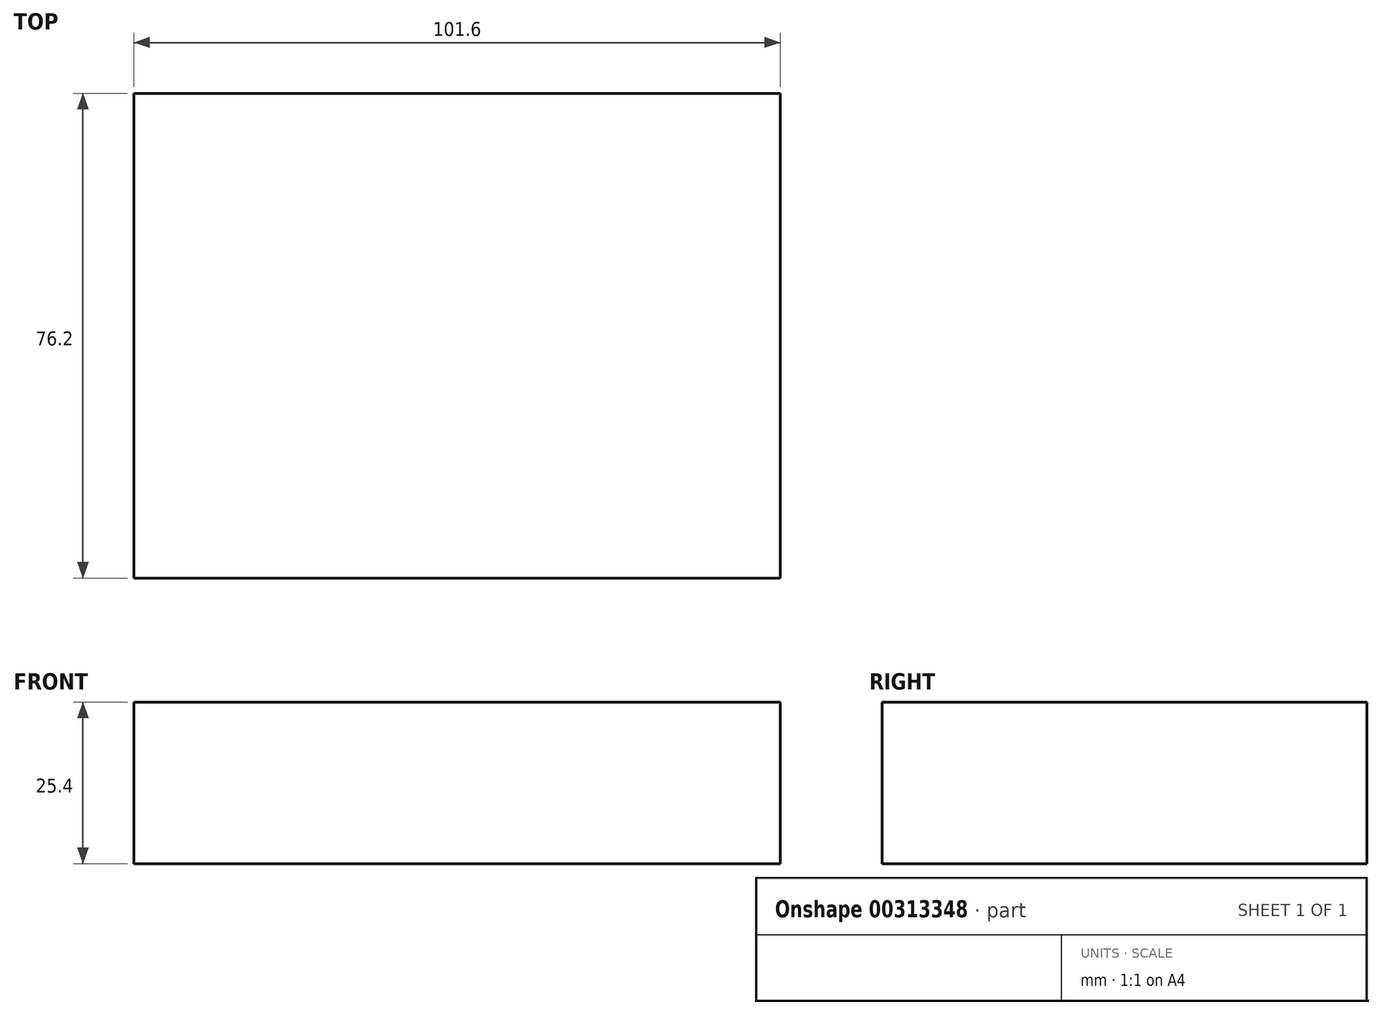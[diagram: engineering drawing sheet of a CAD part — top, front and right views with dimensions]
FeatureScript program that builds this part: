
annotation { "Feature Type Name" : "Feature", "Feature Type Description" : "" }
export const myFeature = defineFeature(function(context is Context, id is Id, definition is map)
    precondition{}
    {
        {
            var Q0;
            Q0=qCreatedBy(makeId("Front.planeOp"),FACE);
            var sketch = newSketch(context, id + "F0", { "sketchPlane" : qUnion([Q0])});
            skLineSegment(sketch, "E0", {"start": v(-46.43, -28.03) * mm, "end": v(55.17, -28.03) * mm});
            skLineSegment(sketch, "E1", {"start": v(-46.43, -28.03) * mm, "end": v(-46.43, -2.63) * mm});
            skLineSegment(sketch, "E2", {"start": v(55.17, -28.03) * mm, "end": v(55.17, -2.63) * mm});
            skLineSegment(sketch, "E3", {"start": v(55.17, -2.63) * mm, "end": v(-46.43, -2.63) * mm});
            skSolve(sketch);
        }
        {
            var Q0;
            Q0=makeQuery(id+"F0.imprint","IMPRINT",FACE,{"disambiguationData":[TD([[makeQuery(id+"F0.imprint","IMPRINT",EDGE,{"derivedFrom":sQuery(id+"F0.wireOp",EDGE,"E0")}),1.0]])]});
            extrude(context, id + "F1", {"entities" : qUnion([Q0]), "depth" : 76.2 * mm});
        }
    });
